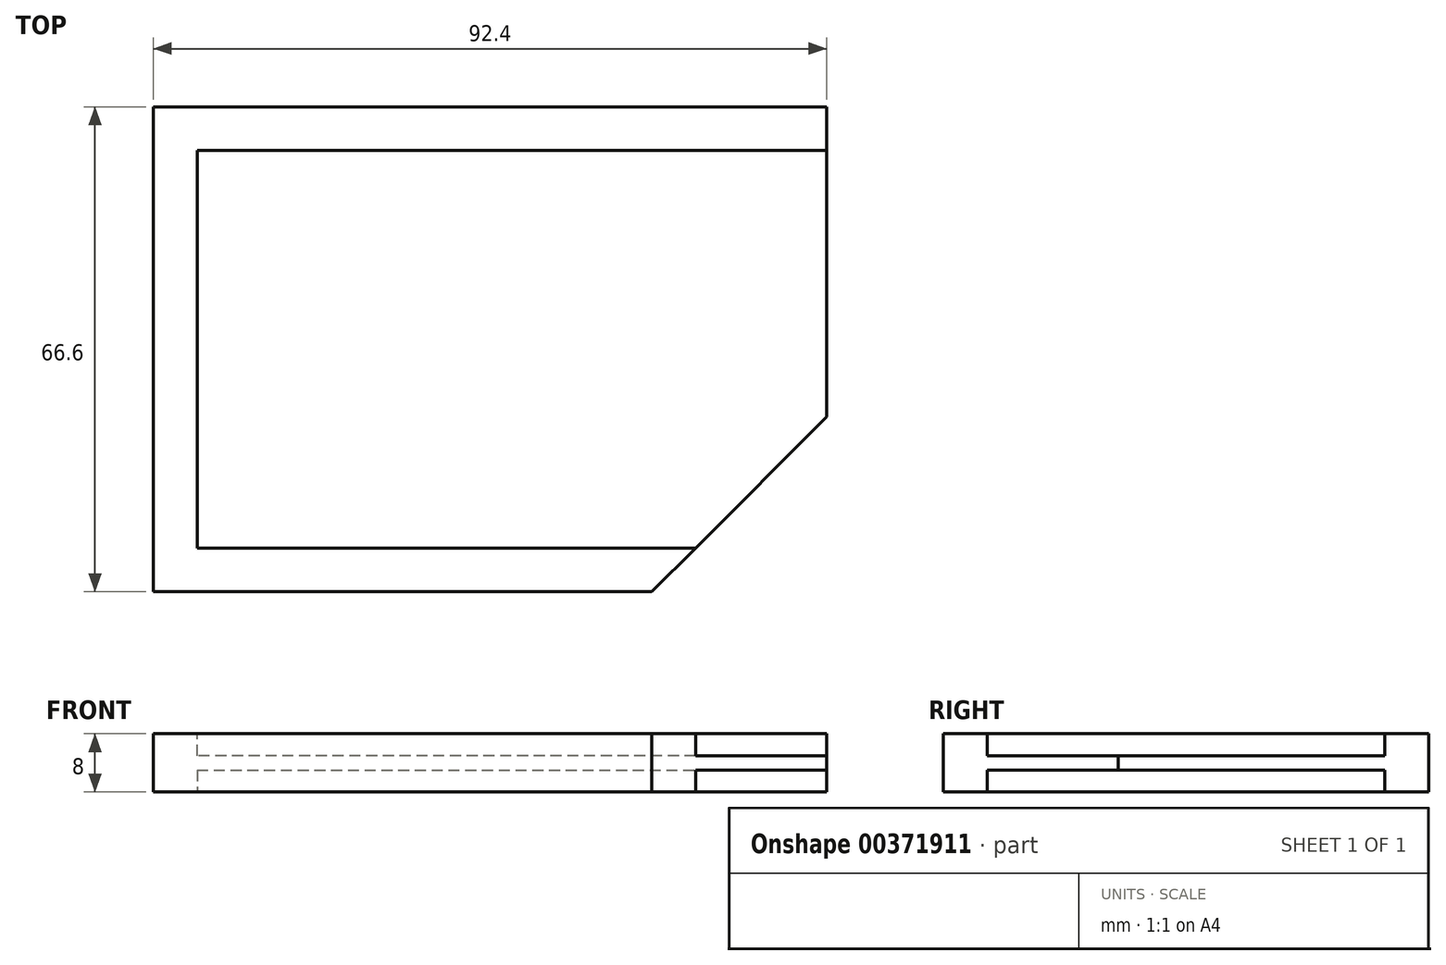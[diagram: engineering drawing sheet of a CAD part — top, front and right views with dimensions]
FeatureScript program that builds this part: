
annotation { "Feature Type Name" : "Feature", "Feature Type Description" : "" }
export const myFeature = defineFeature(function(context is Context, id is Id, definition is map)
    precondition{}
    {
        {
            var Q0;
            Q0=qCreatedBy(makeId("Top.planeOp"),FACE);
            var sketch = newSketch(context, id + "F0", { "sketchPlane" : qUnion([Q0])});
            skLineSegment(sketch, "E0.bottom", {"start": v(-43.2, 27.3) * mm, "end": v(43.2, 27.3) * mm});
            skLineSegment(sketch, "E0.top", {"start": v(-43.2, -27.3) * mm, "end": v(43.2, -27.3) * mm});
            skLineSegment(sketch, "E0.left", {"start": v(-43.2, 27.3) * mm, "end": v(-43.2, -27.3) * mm});
            skLineSegment(sketch, "E0.right", {"start": v(43.2, 27.3) * mm, "end": v(43.2, -27.3) * mm});
            skPoint(sketch, "E0.middle", {"position": v(0, 0) * mm});
            skLineSegment(sketch, "E1.bottom", {"start": v(-49.2, 33.3) * mm, "end": v(49.2, 33.3) * mm});
            skLineSegment(sketch, "E1.top", {"start": v(-49.2, -33.3) * mm, "end": v(49.2, -33.3) * mm});
            skLineSegment(sketch, "E1.left", {"start": v(-49.2, 33.3) * mm, "end": v(-49.2, -33.3) * mm});
            skLineSegment(sketch, "E1.right", {"start": v(49.2, 33.3) * mm, "end": v(49.2, -33.3) * mm});
            skLineSegment(sketch, "E2", {"start": v(43.2, 27.3) * mm, "end": v(43.2, 33.3) * mm});
            skLineSegment(sketch, "E3", {"start": v(43.2, -27.3) * mm, "end": v(43.2, -33.3) * mm});
            skSolve(sketch);
        }
        {
            var Q0;
            Q0=makeQuery(id+"F0.imprint","IMPRINT",FACE,{"disambiguationData":[TD([[makeQuery(id+"F0.imprint","IMPRINT",EDGE,{"derivedFrom":sQuery(id+"F0.wireOp",EDGE,"E0.bottom")}),1.0]])]});
            var Q1;
            Q1=makeQuery(id+"F0.imprint","IMPRINT",FACE,{"disambiguationData":[TD([[makeQuery(id+"F0.imprint","IMPRINT",EDGE,{"derivedFrom":sQuery(id+"F0.wireOp",EDGE,"E0.bottom")}),-1.0]])]});
            extrude(context, id + "F1", {"entities" : qUnion([Q0, Q1]), "depth" : 8 * mm});
        }
        {
            var Q0;
            Q0=makeQuery(id+"F1.opExtrude","CAP_FACE",FACE,{"disambiguationData":[OSD([sQuery(id+"F0.wireOp",EDGE,"E0.right"),sQuery(id+"F0.wireOp",EDGE,"E1.bottom"),sQuery(id+"F0.wireOp",EDGE,"E1.top"),sQuery(id+"F0.wireOp",EDGE,"E1.left"),sQuery(id+"F0.wireOp",EDGE,"E2"),sQuery(id+"F0.wireOp",EDGE,"E3")])],"isStart":false});
            var sketch = newSketch(context, id + "F2", { "sketchPlane" : qUnion([Q0])});
            skLineSegment(sketch, "E4.bottom", {"start": v(43.2, 27.3) * mm, "end": v(-43.2, 27.3) * mm});
            skLineSegment(sketch, "E4.top", {"start": v(43.2, -27.3) * mm, "end": v(-43.2, -27.3) * mm});
            skLineSegment(sketch, "E4.left", {"start": v(43.2, 27.3) * mm, "end": v(43.2, -27.3) * mm});
            skLineSegment(sketch, "E4.right", {"start": v(-43.2, 27.3) * mm, "end": v(-43.2, -27.3) * mm});
            skSolve(sketch);
        }
        {
            var Q0;
            Q0 = qSketchRegion(id + "F2", true);
            extrude(context, id + "F3", {"entities" : qUnion([Q0]), "operationType" : NewBodyOperationType.REMOVE, "oppositeDirection" : true, "depth" : 3 * mm});
        }
        {
            var Q0;
            Q0=makeQuery(id+"F1.opExtrude","CAP_FACE",FACE,{"disambiguationData":[OSD([sQuery(id+"F0.wireOp",EDGE,"E0.right"),sQuery(id+"F0.wireOp",EDGE,"E1.bottom"),sQuery(id+"F0.wireOp",EDGE,"E1.top"),sQuery(id+"F0.wireOp",EDGE,"E1.left"),sQuery(id+"F0.wireOp",EDGE,"E2"),sQuery(id+"F0.wireOp",EDGE,"E3")])],"isStart":true});
            var sketch = newSketch(context, id + "F4", { "sketchPlane" : qUnion([Q0])});
            skLineSegment(sketch, "E5.0.0", {"start": v(-43.2, 27.3) * mm, "end": v(43.2, 27.3) * mm});
            skLineSegment(sketch, "E5.0.1", {"start": v(43.2, 27.3) * mm, "end": v(43.2, -27.3) * mm});
            skLineSegment(sketch, "E5.0.2", {"start": v(43.2, -27.3) * mm, "end": v(-43.2, -27.3) * mm});
            skLineSegment(sketch, "E5.0.3", {"start": v(-43.2, -27.3) * mm, "end": v(-43.2, 27.3) * mm});
            skSolve(sketch);
        }
        {
            var Q0;
            Q0 = qSketchRegion(id + "F4", true);
            extrude(context, id + "F5", {"entities" : qUnion([Q0]), "operationType" : NewBodyOperationType.REMOVE, "oppositeDirection" : true, "depth" : 3 * mm});
        }
        {
            var Q0;
            Q0=makeQuery(id+"F1.opExtrude","CAP_FACE",FACE,{"disambiguationData":[OSD([sQuery(id+"F0.wireOp",EDGE,"E0.right"),sQuery(id+"F0.wireOp",EDGE,"E1.bottom"),sQuery(id+"F0.wireOp",EDGE,"E1.top"),sQuery(id+"F0.wireOp",EDGE,"E1.left"),sQuery(id+"F0.wireOp",EDGE,"E2"),sQuery(id+"F0.wireOp",EDGE,"E3")])],"isStart":true});
            var sketch = newSketch(context, id + "F6", { "sketchPlane" : qUnion([Q0])});
            skLineSegment(sketch, "E6", {"start": v(19.2, 33.3) * mm, "end": v(43.2, 9.3) * mm});
            skLineSegment(sketch, "E7", {"start": v(43.2, 9.3) * mm, "end": v(43.2, 33.3) * mm});
            skLineSegment(sketch, "E8", {"start": v(43.2, 33.3) * mm, "end": v(19.2, 33.3) * mm});
            skSolve(sketch);
        }
        {
            var Q0;
            Q0 = qSketchRegion(id + "F6", true);
            extrude(context, id + "F7", {"entities" : qUnion([Q0]), "operationType" : NewBodyOperationType.REMOVE, "oppositeDirection" : true, "depth" : 25 * mm});
        }
    });
